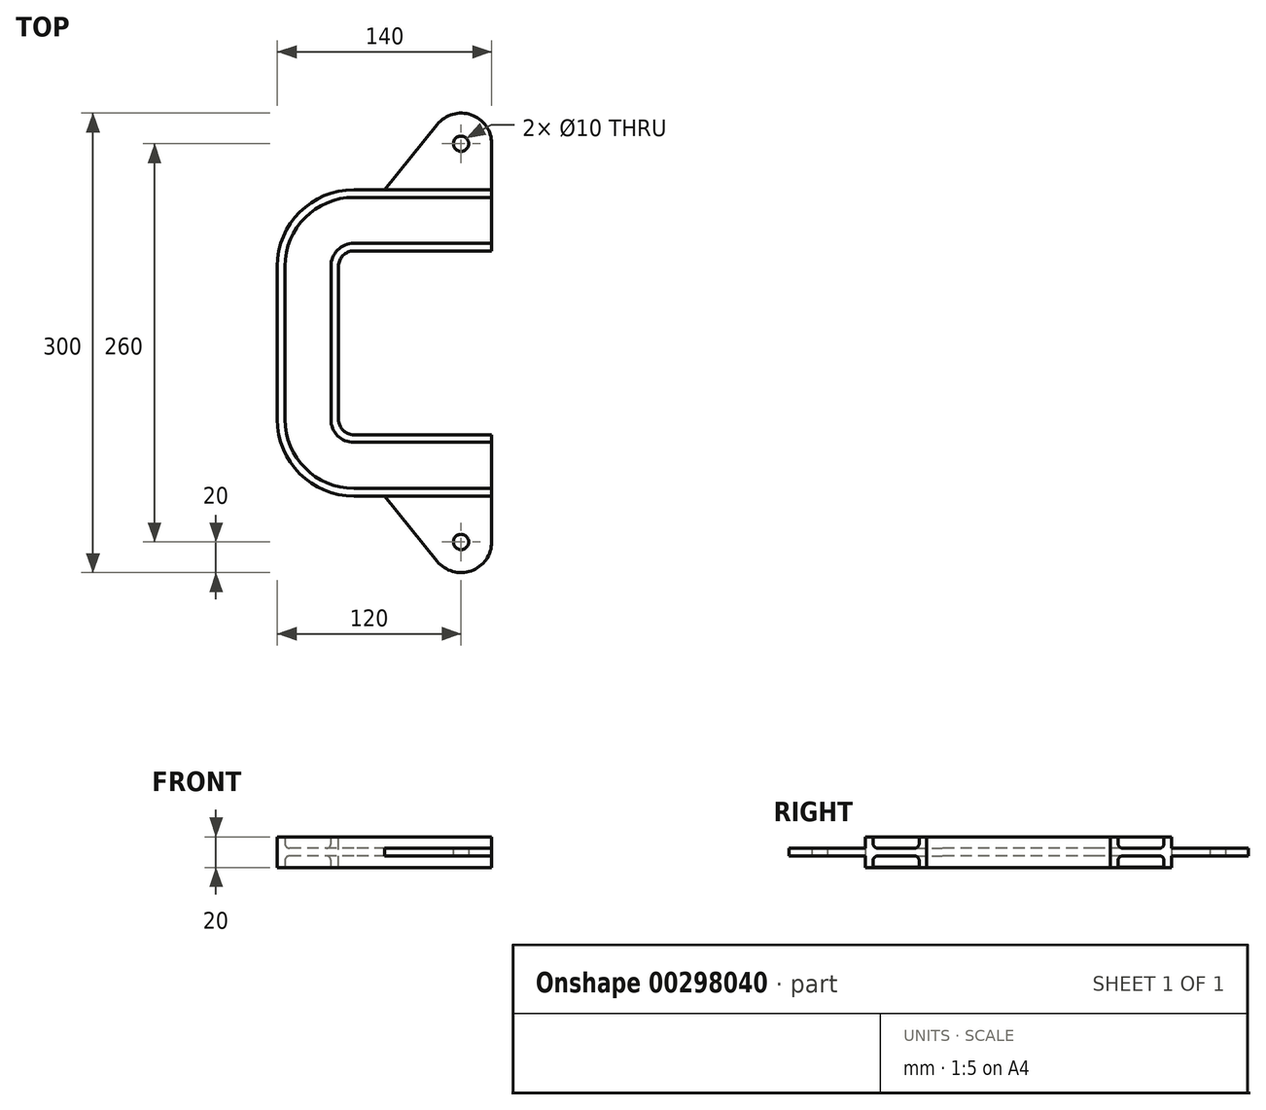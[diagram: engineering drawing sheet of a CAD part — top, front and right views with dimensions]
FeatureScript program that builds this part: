
annotation { "Feature Type Name" : "Feature", "Feature Type Description" : "" }
export const myFeature = defineFeature(function(context is Context, id is Id, definition is map)
    precondition{}
    {
        {
            var Q0;
            Q0=qCreatedBy(makeId("Top.planeOp"),FACE);
            var sketch = newSketch(context, id + "F0", { "sketchPlane" : qUnion([Q0])});
            skArc(sketch, "E0", {"start": v(-90, 60) * mm, "mid": v(-97.07, 57.07) * mm, "end": v(-100, 50) * mm});
            skLineSegment(sketch, "E1", {"start": v(-100, 50) * mm, "end": v(-100, 0) * mm});
            skLineSegment(sketch, "E2", {"start": v(-90, 60) * mm, "end": v(0, 60) * mm});
            skSolve(sketch);
        }
        {
            var Q0;
            Q0=qCreatedBy(makeId("Right.planeOp"),FACE);
            var sketch = newSketch(context, id + "F1", { "sketchPlane" : qUnion([Q0])});
            skLineSegment(sketch, "E3", {"start": v(100, -10) * mm, "end": v(100, 10) * mm});
            skLineSegment(sketch, "E4", {"start": v(100, 10) * mm, "end": v(95, 10) * mm});
            skLineSegment(sketch, "E5", {"start": v(95, 10) * mm, "end": v(95, 5.5) * mm});
            skLineSegment(sketch, "E6", {"start": v(92, 2.5) * mm, "end": v(68, 2.5) * mm});
            skLineSegment(sketch, "E7", {"start": v(65, 5.5) * mm, "end": v(65, 10) * mm});
            skLineSegment(sketch, "E8", {"start": v(65, 10) * mm, "end": v(60, 10) * mm});
            skLineSegment(sketch, "E9", {"start": v(60, -10) * mm, "end": v(65, -10) * mm});
            skLineSegment(sketch, "E10", {"start": v(65, -10) * mm, "end": v(65, -5.5) * mm});
            skLineSegment(sketch, "E11", {"start": v(68, -2.5) * mm, "end": v(92, -2.5) * mm});
            skPoint(sketch, "E12.visualSharp", {"position": v(95, 2.5) * mm});
            skArc(sketch, "E12.filletArc", {"start": v(92, 2.5) * mm, "mid": v(94.12, 3.38) * mm, "end": v(95, 5.5) * mm});
            skPoint(sketch, "E13.visualSharp", {"position": v(65, 2.5) * mm});
            skArc(sketch, "E13.filletArc", {"start": v(65, 5.5) * mm, "mid": v(65.88, 3.38) * mm, "end": v(68, 2.5) * mm});
            skPoint(sketch, "E14.visualSharp", {"position": v(65, -2.5) * mm});
            skArc(sketch, "E14.filletArc", {"start": v(68, -2.5) * mm, "mid": v(65.88, -3.38) * mm, "end": v(65, -5.5) * mm});
            skPoint(sketch, "E15.visualSharp", {"position": v(95, -2.5) * mm});
            skArc(sketch, "E15.filletArc", {"start": v(95, -5.5) * mm, "mid": v(94.12, -3.38) * mm, "end": v(92, -2.5) * mm});
            skLineSegment(sketch, "E16", {"start": v(60, -10) * mm, "end": v(60, 0) * mm});
            skLineSegment(sketch, "E17", {"start": v(60, 0) * mm, "end": v(60, 10) * mm});
            skLineSegment(sketch, "E18", {"start": v(95, -5.5) * mm, "end": v(95, -9.87) * mm});
            skLineSegment(sketch, "E19", {"start": v(95, -9.87) * mm, "end": v(100, -10) * mm});
            skSolve(sketch);
        }
        {
            var Q0;
            Q0=makeQuery(id+"F1.imprint","IMPRINT",FACE,{"disambiguationData":[TD([[makeQuery(id+"F1.imprint","IMPRINT",EDGE,{"derivedFrom":sQuery(id+"F1.wireOp",EDGE,"E3")}),1.0]])]});
            var Q1;
            Q1=sQuery(id+"F0.wireOp",EDGE,"E2");
            var Q2;
            Q2=sQuery(id+"F0.wireOp",EDGE,"E0");
            var Q3;
            Q3=sQuery(id+"F0.wireOp",EDGE,"E1");
            sweep(context, id + "F2", {"profiles" : qUnion([Q0]), "path" : qUnion([Q1, Q2, Q3])});
        }
        {
            var Q0;
            Q0=makeQuery(id+"F2.opSweep","SWEPT_BODY",BODY,{"disambiguationData":[OSD([sQuery(id+"F0.wireOp",EDGE,"E1"),sQuery(id+"F1.wireOp",EDGE,"E3"),sQuery(id+"F1.wireOp",EDGE,"E4"),sQuery(id+"F1.wireOp",EDGE,"E5"),sQuery(id+"F1.wireOp",EDGE,"E6"),sQuery(id+"F1.wireOp",EDGE,"E7"),sQuery(id+"F1.wireOp",EDGE,"E8"),sQuery(id+"F1.wireOp",EDGE,"E9"),sQuery(id+"F1.wireOp",EDGE,"E10"),sQuery(id+"F1.wireOp",EDGE,"E11"),sQuery(id+"F1.wireOp",EDGE,"E12.filletArc"),sQuery(id+"F1.wireOp",EDGE,"E13.filletArc"),sQuery(id+"F1.wireOp",EDGE,"E14.filletArc"),sQuery(id+"F1.wireOp",EDGE,"E15.filletArc"),sQuery(id+"F1.wireOp",EDGE,"E16"),sQuery(id+"F1.wireOp",EDGE,"E17"),sQuery(id+"F1.wireOp",EDGE,"E18"),sQuery(id+"F1.wireOp",EDGE,"E19")])]});
            var Q1;
            Q1=qCreatedBy(makeId("Front.planeOp"),FACE);
            mirror(context, id + "F3", {"operationType" : NewBodyOperationType.ADD, "entities" : qUnion([Q0]), "mirrorPlane" : qUnion([Q1])});
        }
        {
            var Q0;
            Q0=qCreatedBy(makeId("Top.planeOp"),FACE);
            var sketch = newSketch(context, id + "F4", { "sketchPlane" : qUnion([Q0])});
            skLineSegment(sketch, "E20", {"start": v(0, 100) * mm, "end": v(0, 130) * mm});
            skLineSegment(sketch, "E21", {"start": v(-35.55, 142.58) * mm, "end": v(-70, 100) * mm});
            skLineSegment(sketch, "E22", {"start": v(-70, 100) * mm, "end": v(0, 100) * mm});
            skPoint(sketch, "E23.visualSharp", {"position": v(42.88, 68.96) * mm});
            skArc(sketch, "E23.filletArc", {"start": v(0, 130) * mm, "mid": v(-13.33, 148.85) * mm, "end": v(-35.55, 142.58) * mm});
            skCircle(sketch, "E24", {"center": v(-20, 130) * mm, "radius": 5 * mm});
            skLineSegment(sketch, "E25.MirrorCS", {"start": v(0, -100) * mm, "end": v(0, -130) * mm});
            skCircle(sketch, "E26.MirrorC", {"center": v(-20, -130) * mm, "radius": 5 * mm});
            skArc(sketch, "E27.MirrorCS", {"start": v(0, -130) * mm, "mid": v(-13.33, -148.85) * mm, "end": v(-35.55, -142.58) * mm});
            skLineSegment(sketch, "E28.MirrorCS", {"start": v(-70, -100) * mm, "end": v(0, -100) * mm});
            skLineSegment(sketch, "E29.MirrorCS", {"start": v(-35.55, -142.58) * mm, "end": v(-70, -100) * mm});
            skSolve(sketch);
        }
        {
            var Q0;
            Q0=makeQuery(id+"F4.imprint","IMPRINT",FACE,{"disambiguationData":[TD([[makeQuery(id+"F4.imprint","IMPRINT",EDGE,{"derivedFrom":sQuery(id+"F4.wireOp",EDGE,"E20")}),1.0]])]});
            var Q1;
            Q1=makeQuery(id+"F4.imprint","IMPRINT",FACE,{"disambiguationData":[TD([[makeQuery(id+"F4.imprint","IMPRINT",EDGE,{"derivedFrom":sQuery(id+"F4.wireOp",EDGE,"E28.MirrorCS")}),-1.0]])]});
            extrude(context, id + "F5", {"entities" : qUnion([Q0, Q1]), "operationType" : NewBodyOperationType.ADD, "endBound" : BoundingType.SYMMETRIC, "depth" : 5 * mm});
        }
    });
